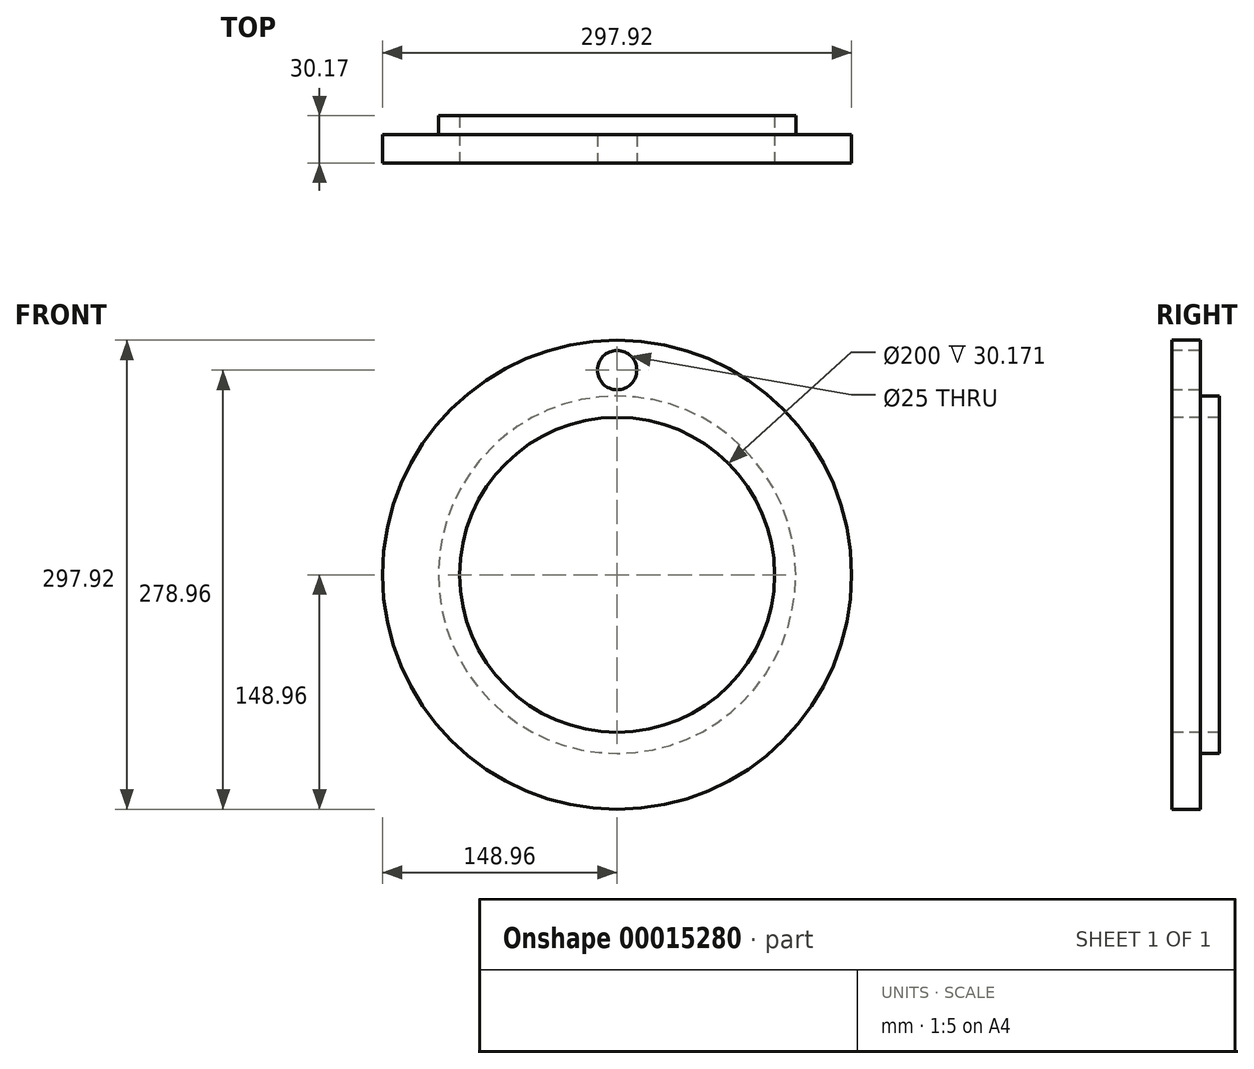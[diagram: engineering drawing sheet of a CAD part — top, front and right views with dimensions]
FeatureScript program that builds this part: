
annotation { "Feature Type Name" : "Feature", "Feature Type Description" : "" }
export const myFeature = defineFeature(function(context is Context, id is Id, definition is map)
    precondition{}
    {
        {
            var Q0;
            Q0=qCreatedBy(makeId("Right.planeOp"),FACE);
            var sketch = newSketch(context, id + "F0", { "sketchPlane" : qUnion([Q0])});
            skLineSegment(sketch, "E0", {"start": v(0, 0) * mm, "end": v(110.25, 0) * mm});
            skPoint(sketch, "E1.end.orphan", {"position": v(0, 100) * mm});
            skLineSegment(sketch, "E2", {"start": v(0, 100) * mm, "end": v(0, 148.96) * mm});
            skLineSegment(sketch, "E3", {"start": v(0, 148.96) * mm, "end": v(18.03, 148.96) * mm});
            skLineSegment(sketch, "E4", {"start": v(18.03, 148.96) * mm, "end": v(18.03, 113.47) * mm});
            skLineSegment(sketch, "E5", {"start": v(18.03, 113.47) * mm, "end": v(30.17, 113.47) * mm});
            skLineSegment(sketch, "E6", {"start": v(30.17, 113.47) * mm, "end": v(30.17, 100) * mm});
            skLineSegment(sketch, "E7", {"start": v(30.17, 100) * mm, "end": v(0, 100) * mm});
            skSolve(sketch);
        }
        {
            var Q0;
            Q0=makeQuery(id+"F0.imprint","IMPRINT",FACE,{"disambiguationData":[TD([[makeQuery(id+"F0.imprint","IMPRINT",EDGE,{"derivedFrom":sQuery(id+"F0.wireOp",EDGE,"E2")}),-1.0]])]});
            var Q1;
            Q1=sQuery(id+"F0.wireOp",EDGE,"E0");
            revolve(context, id + "F1", {"entities" : qUnion([Q0]), "axis" : qUnion([Q1]), "revolveType" : RevolveType.FULL});
        }
        {
            var Q0;
            Q0=makeQuery(id+"F1.opRevolve","SWEPT_FACE",FACE,{"disambiguationData":[OSD([sQuery(id+"F0.wireOp",EDGE,"E2")])]});
            var sketch = newSketch(context, id + "F2", { "sketchPlane" : qUnion([Q0])});
            skCircle(sketch, "E8", {"center": v(0, 130) * mm, "radius": 12.5 * mm});
            skLineSegment(sketch, "E9", {"start": v(0, 130) * mm, "end": v(0, 0) * mm});
            skLineSegment(sketch, "E10", {"start": v(0, 0) * mm, "end": v(0, 130) * mm});
            skCircle(sketch, "E11", {"center": v(0, 0) * mm, "radius": 130 * mm});
            skSolve(sketch);
        }
        {
            var Q0;
            {var subQ0=sQuery(id+"F2.wireOp",EDGE,"E11");var subQ1=sQuery(id+"F2.wireOp",EDGE,"E8");var subQ2=makeQuery(id+"F2.imprint","INTERSECT",VERTEX,{"disambiguationData":[OD(0.0)],"derivedFrom":[subQ1,subQ0]});Q0=makeQuery(id+"F2.imprint","IMPRINT",FACE,{"disambiguationData":[TD([[makeQuery(id+"F2.imprint","IMPRINT",EDGE,{"disambiguationData":[TD([[subQ2,1.0]])],"derivedFrom":subQ1}),1.0]])]});}
            var Q1;
            {var subQ1=sQuery(id+"F2.wireOp",EDGE,"E8");var subQ3=sQuery(id+"F2.wireOp",EDGE,"E10");var subQ5=makeQuery(id+"F2.imprint","INTERSECT",VERTEX,{"derivedFrom":[subQ1,subQ3]});Q1=makeQuery(id+"F2.imprint","IMPRINT",FACE,{"disambiguationData":[TD([[makeQuery(id+"F2.imprint","IMPRINT",EDGE,{"disambiguationData":[TD([[subQ5,-1.0]])],"derivedFrom":subQ1}),1.0]])]});}
            extrude(context, id + "F3", {"entities" : qUnion([Q0, Q1]), "operationType" : NewBodyOperationType.REMOVE, "oppositeDirection" : true, "depth" : 25 * mm});
        }
    });
